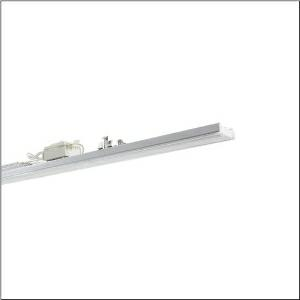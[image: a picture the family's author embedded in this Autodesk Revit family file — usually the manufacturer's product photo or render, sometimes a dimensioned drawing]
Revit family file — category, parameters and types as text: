
# Revit family: licross_21_recessed_mo_52tl11de45xg
name_source: partatom
category: Lighting Fixtures
units: mm (PartAtom-declared; Revit-internal decimal feet)

## family parameters
Cut with Voids When Loaded = No
Host = Face
Light Source = No
Part Type = Normal
Room Calculation Point = No
Round Connector Dimension = Use Diameter
Shared = No

## types (1)
- --- (1 x LED, 5060 lm, 29.9 W, 4000K)
    Apparent Load = 30 VA
    CIE Flux Codes = 89 96 99 100 100
    Color Rendering = 80
    Color Temperature = 4000K
    Default Elevation = 1800 mm
    Description = Licross 21 Recessed MO, luminaire insert, of sheet steel, galvanised, coil coated, white, length: 750mm, width: 66mm, height: 67mm, LED rated luminous flux: 5.060lm, light colour: 840, SDCM (Standard Deviation of Colour Matching)MacAdam ≤ 3 SDCM (initial), control gear: DALI 2, with plug, 5-pole, with phase selection, mains connection: 220..240V, AC, 50/60Hz, rated input power: 30W, internal wiring halogen-free, primary light control with lens, of plastic, primary optical cover: cover, of PMMA, light emission: direct distribution, primary light characteristic: symmetric, protection rating (complete): IP40, insulation class (complete): insulation class I (protective earthing), certification: CE, ENEC, VDE, UKCA, protection symbol: D if used in an environment without relevant dust loads with corresponding accessories, impact resistance: IK06, permissible ambient temperature for indoor applications: -25..+35°C, corresponds to IFS (International Featured Standards) requirements for safety and quality in the food industry, reducing of maximum allowable ambient temperature of 5°C with ceiling mounting, LABS conformity tested according to VDMA 24364:2018-05, The light source and the operating device comply with the requirements of the Ecodesign Regulation (EU) 2019/2020 and are replaceable in accordance with this regulation, packaging unit: 1 piece
    Height = 58 mm
    Lamp = 1 x LED
    Lamp Light Flux = 5060 lm
    Lamp Power = 29.9 W
    Lamp count = 1
    Length = 750 mm
    Luminous efficacy = 169 lm/W
    Manufacturer = Siteco
    ModVariant = No
    Model = 52TL11DE45XG
    Mounting Place = Ceiling
    Mounting Type = Pendant
    Number of Poles = 1
    OnlyDefault = Yes
    Power Factor = 1
    Product Name = Licross 21 Recessed MO
    Product group = luminaire insert | ceiling pendant
    ProductGroupID = 901
    Protection Class = Protection class I
    Protection Degree = IP 40
    RLX_Detail_Level = 1
    RLX_Emergency_Light_Flux = 0 lm
    RLX_Emergency_Type = 0
    RLX_Emergency_Type_DB = No
    RlxData = <blob elided: 29153 chars, md5=48b1b1d9>
    Socket = socket
    Standby Power = 0 W
    System Light Flux = 5060 lm
    System Power = 30 W
    Type Comments = factory setting: luminous flux: 100 % | dim-lin: 254 | 390 mA
    Type Image = l_1296930.jpg
    URL = http://relux.com
    VarID = @adj_127301
    Voltage = 0 V
    Weight = 0.00 kg
    Width = 66 mm

## geometry (parser evidence)
native form markers: Blend x4, Sweep x10
no freeform markers — native parametric forms only
